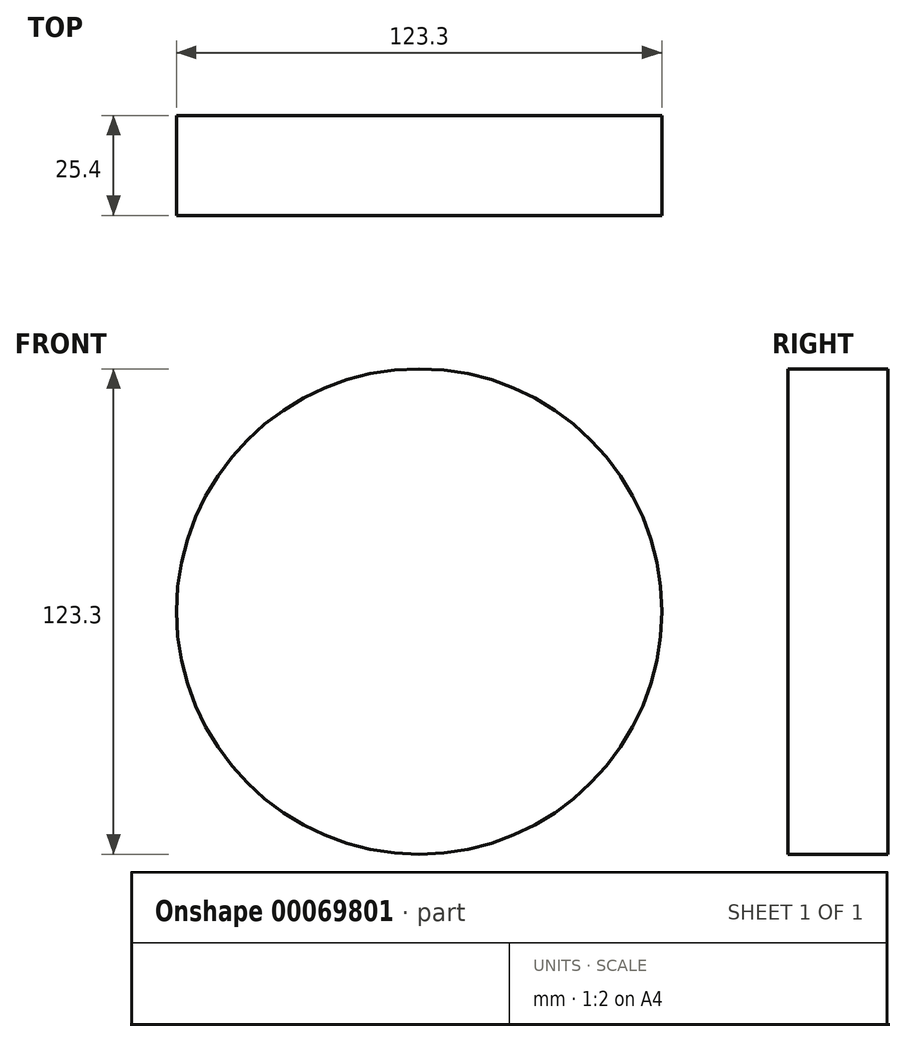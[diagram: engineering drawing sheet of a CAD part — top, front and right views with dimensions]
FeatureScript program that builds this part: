
annotation { "Feature Type Name" : "Feature", "Feature Type Description" : "" }
export const myFeature = defineFeature(function(context is Context, id is Id, definition is map)
    precondition{}
    {
        {
            var Q0;
            Q0=qCreatedBy(makeId("Front.planeOp"),FACE);
            var sketch = newSketch(context, id + "F0", { "sketchPlane" : qUnion([Q0])});
            skCircle(sketch, "E0", {"center": v(0, 0) * mm, "radius": 61.65 * mm});
            skSolve(sketch);
        }
        {
            var Q0;
            Q0=makeQuery(id+"F0.imprint","IMPRINT",FACE,{"disambiguationData":[TD([[makeQuery(id+"F0.imprint","IMPRINT",EDGE,{"derivedFrom":sQuery(id+"F0.wireOp",EDGE,"E0")}),1.0]])]});
            extrude(context, id + "F1", {"entities" : qUnion([Q0]), "depth" : 25.4 * mm});
        }
    });
